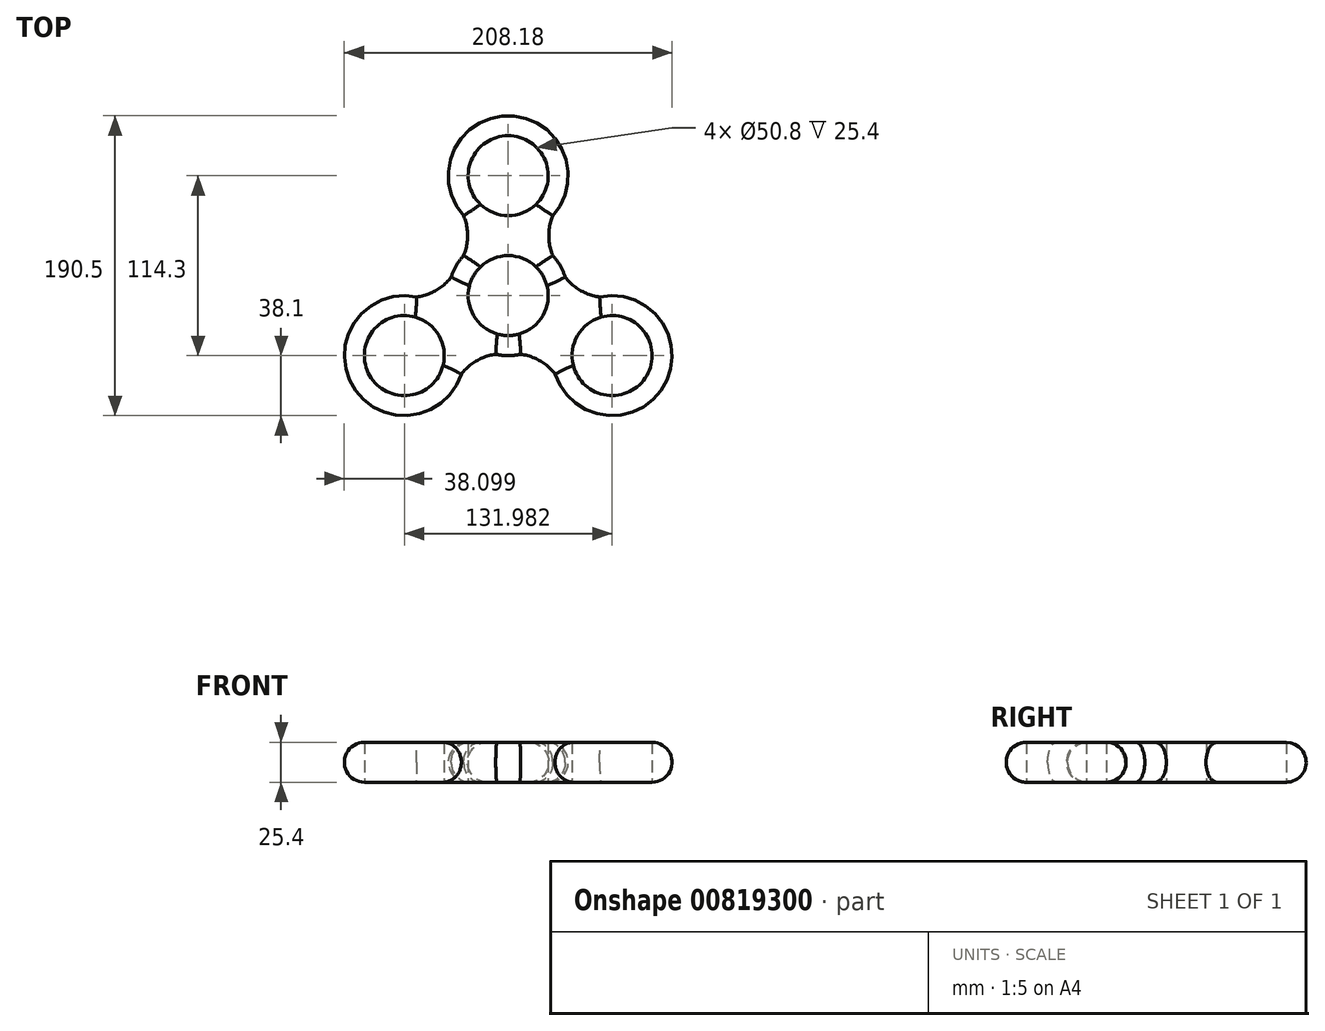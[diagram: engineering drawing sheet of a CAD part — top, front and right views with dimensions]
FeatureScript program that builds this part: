
annotation { "Feature Type Name" : "Feature", "Feature Type Description" : "" }
export const myFeature = defineFeature(function(context is Context, id is Id, definition is map)
    precondition{}
    {
        {
            var Q0;
            Q0=qCreatedBy(makeId("Top.planeOp"),FACE);
            var sketch = newSketch(context, id + "F0", { "sketchPlane" : qUnion([Q0])});
            skCircle(sketch, "E0", {"center": v(0, 0) * mm, "radius": 38.1 * mm});
            skCircle(sketch, "E1", {"center": v(0, 76.2) * mm, "radius": 38.1 * mm});
            skCircle(sketch, "E2.1.0", {"center": v(-66, -38.1) * mm, "radius": 38.1 * mm});
            skCircle(sketch, "E2.2.0", {"center": v(66, -38.1) * mm, "radius": 38.1 * mm});
            skLineSegment(sketch, "E3", {"start": v(0, 38.1) * mm, "end": v(78.67, 38.1) * mm, "construction": true});
            skLineSegment(sketch, "E4", {"start": v(0, 38.1) * mm, "end": v(-78.67, 38.1) * mm, "construction": true});
            skArc(sketch, "E5", {"start": v(28.32, 50.71) * mm, "mid": v(25.78, 38.1) * mm, "end": v(28.32, 25.49) * mm});
            skLineSegment(sketch, "E6", {"start": v(0, 38.1) * mm, "end": v(0, 50.71) * mm, "construction": true});
            skLineSegment(sketch, "E7", {"start": v(0, 50.71) * mm, "end": v(0, 38.1) * mm, "construction": true});
            skLineSegment(sketch, "E8", {"start": v(0, 25.49) * mm, "end": v(0, 38.1) * mm, "construction": true});
            skArc(sketch, "E9", {"start": v(-28.32, 25.49) * mm, "mid": v(-25.78, 38.1) * mm, "end": v(-28.32, 50.71) * mm});
            skArc(sketch, "E10.1.0", {"start": v(-58.08, -0.83) * mm, "mid": v(-45.89, 3.28) * mm, "end": v(-36.23, 11.78) * mm});
            skArc(sketch, "E10.1.1", {"start": v(-7.91, -37.27) * mm, "mid": v(-20.1, -41.38) * mm, "end": v(-29.76, -49.88) * mm});
            skArc(sketch, "E10.2.0", {"start": v(29.76, -49.88) * mm, "mid": v(20.1, -41.38) * mm, "end": v(7.91, -37.27) * mm});
            skArc(sketch, "E10.2.1", {"start": v(36.23, 11.78) * mm, "mid": v(45.89, 3.28) * mm, "end": v(58.08, -0.83) * mm});
            skCircle(sketch, "E11", {"center": v(0, 0) * mm, "radius": 25.4 * mm});
            skCircle(sketch, "E12", {"center": v(0, 76.2) * mm, "radius": 25.4 * mm});
            skCircle(sketch, "E13.1.0", {"center": v(-66, -38.1) * mm, "radius": 25.4 * mm});
            skCircle(sketch, "E13.2.0", {"center": v(66, -38.1) * mm, "radius": 25.4 * mm});
            skSolve(sketch);
        }
        {
            var Q0;
            Q0=makeQuery(id+"F0.imprint","IMPRINT",FACE,{"disambiguationData":[TD([[makeQuery(id+"F0.imprint","IMPRINT",EDGE,{"derivedFrom":sQuery(id+"F0.wireOp",EDGE,"E12")}),-1.0]])]});
            var Q1;
            {var subQ0=sQuery(id+"F0.wireOp",EDGE,"E9");Q1=makeQuery(id+"F0.imprint","IMPRINT",FACE,{"disambiguationData":[TD([[makeQuery(id+"F0.imprint","IMPRINT",EDGE,{"derivedFrom":subQ0}),-1.0]])]});}
            var Q2;
            {var subQ0=sQuery(id+"F0.wireOp",EDGE,"E5");Q2=makeQuery(id+"F0.imprint","IMPRINT",FACE,{"disambiguationData":[TD([[makeQuery(id+"F0.imprint","IMPRINT",EDGE,{"derivedFrom":subQ0}),-1.0]])]});}
            var Q3;
            Q3=makeQuery(id+"F0.imprint","IMPRINT",FACE,{"disambiguationData":[TD([[makeQuery(id+"F0.imprint","IMPRINT",EDGE,{"derivedFrom":sQuery(id+"F0.wireOp",EDGE,"E11")}),-1.0]])]});
            var Q4;
            {var subQ0=sQuery(id+"F0.wireOp",EDGE,"E10.2.1");Q4=makeQuery(id+"F0.imprint","IMPRINT",FACE,{"disambiguationData":[TD([[makeQuery(id+"F0.imprint","IMPRINT",EDGE,{"derivedFrom":subQ0}),-1.0]])]});}
            var Q5;
            {var subQ0=sQuery(id+"F0.wireOp",EDGE,"E10.2.0");Q5=makeQuery(id+"F0.imprint","IMPRINT",FACE,{"disambiguationData":[TD([[makeQuery(id+"F0.imprint","IMPRINT",EDGE,{"derivedFrom":subQ0}),-1.0]])]});}
            var Q6;
            Q6=makeQuery(id+"F0.imprint","IMPRINT",FACE,{"disambiguationData":[TD([[makeQuery(id+"F0.imprint","IMPRINT",EDGE,{"derivedFrom":sQuery(id+"F0.wireOp",EDGE,"E13.2.0")}),-1.0]])]});
            var Q7;
            Q7=makeQuery(id+"F0.imprint","IMPRINT",FACE,{"disambiguationData":[TD([[makeQuery(id+"F0.imprint","IMPRINT",EDGE,{"derivedFrom":sQuery(id+"F0.wireOp",EDGE,"E13.1.0")}),-1.0]])]});
            var Q8;
            {var subQ0=sQuery(id+"F0.wireOp",EDGE,"E10.1.0");Q8=makeQuery(id+"F0.imprint","IMPRINT",FACE,{"disambiguationData":[TD([[makeQuery(id+"F0.imprint","IMPRINT",EDGE,{"derivedFrom":subQ0}),-1.0]])]});}
            var Q9;
            {var subQ0=sQuery(id+"F0.wireOp",EDGE,"E10.1.1");Q9=makeQuery(id+"F0.imprint","IMPRINT",FACE,{"disambiguationData":[TD([[makeQuery(id+"F0.imprint","IMPRINT",EDGE,{"derivedFrom":subQ0}),-1.0]])]});}
            extrude(context, id + "F1", {"entities" : qUnion([Q0, Q1, Q2, Q3, Q4, Q5, Q6, Q7, Q8, Q9]), "depth" : 25.4 * mm, "offsetDistance" : 25.4 * mm});
        }
        {
            var Q0;
            Q0=makeQuery(id+"F1.opExtrude","CAP_EDGE",EDGE,{"disambiguationData":[OSD([sQuery(id+"F0.wireOp",EDGE,"E2.1.0")])],"isStart":false});
            var Q1;
            Q1=makeQuery(id+"F1.opExtrude","CAP_EDGE",EDGE,{"disambiguationData":[OSD([sQuery(id+"F0.wireOp",EDGE,"E10.1.1")])],"isStart":false});
            var Q2;
            {var subQ0=sQuery(id+"F0.wireOp",EDGE,"E0");Q2=makeQuery(id+"F1.opExtrude","CAP_EDGE",EDGE,{"disambiguationData":[OSD([subQ0]),TDD([makeQuery(id+"F0.imprint","IMPRINT",EDGE,{"disambiguationData":[TD([[makeQuery(id+"F0.imprint","INTERSECT",VERTEX,{"derivedFrom":[subQ0,sQuery(id+"F0.wireOp",EDGE,"E10.1.1")]}),-1.0]])],"derivedFrom":subQ0})])],"isStart":false});}
            var Q3;
            Q3=makeQuery(id+"F1.opExtrude","CAP_EDGE",EDGE,{"disambiguationData":[OSD([sQuery(id+"F0.wireOp",EDGE,"E10.2.0")])],"isStart":false});
            var Q4;
            Q4=makeQuery(id+"F1.opExtrude","CAP_EDGE",EDGE,{"disambiguationData":[OSD([sQuery(id+"F0.wireOp",EDGE,"E2.2.0")])],"isStart":false});
            var Q5;
            Q5=makeQuery(id+"F1.opExtrude","CAP_EDGE",EDGE,{"disambiguationData":[OSD([sQuery(id+"F0.wireOp",EDGE,"E10.2.1")])],"isStart":false});
            var Q6;
            {var subQ0=sQuery(id+"F0.wireOp",EDGE,"E0");Q6=makeQuery(id+"F1.opExtrude","CAP_EDGE",EDGE,{"disambiguationData":[OSD([subQ0]),TDD([makeQuery(id+"F0.imprint","IMPRINT",EDGE,{"disambiguationData":[TD([[makeQuery(id+"F0.imprint","INTERSECT",VERTEX,{"derivedFrom":[subQ0,sQuery(id+"F0.wireOp",EDGE,"E5")]}),1.0]])],"derivedFrom":subQ0})])],"isStart":false});}
            var Q7;
            Q7=makeQuery(id+"F1.opExtrude","CAP_EDGE",EDGE,{"disambiguationData":[OSD([sQuery(id+"F0.wireOp",EDGE,"E5")])],"isStart":false});
            var Q8;
            Q8=makeQuery(id+"F1.opExtrude","CAP_EDGE",EDGE,{"disambiguationData":[OSD([sQuery(id+"F0.wireOp",EDGE,"E1")])],"isStart":false});
            var Q9;
            Q9=makeQuery(id+"F1.opExtrude","CAP_EDGE",EDGE,{"disambiguationData":[OSD([sQuery(id+"F0.wireOp",EDGE,"E9")])],"isStart":false});
            var Q10;
            {var subQ0=sQuery(id+"F0.wireOp",EDGE,"E0");Q10=makeQuery(id+"F1.opExtrude","CAP_EDGE",EDGE,{"disambiguationData":[OSD([subQ0]),TDD([makeQuery(id+"F0.imprint","IMPRINT",EDGE,{"disambiguationData":[TD([[makeQuery(id+"F0.imprint","INTERSECT",VERTEX,{"derivedFrom":[subQ0,sQuery(id+"F0.wireOp",EDGE,"E9")]}),-1.0]])],"derivedFrom":subQ0})])],"isStart":false});}
            var Q11;
            Q11=makeQuery(id+"F1.opExtrude","CAP_EDGE",EDGE,{"disambiguationData":[OSD([sQuery(id+"F0.wireOp",EDGE,"E10.1.0")])],"isStart":false});
            var Q12;
            {var subQ0=sQuery(id+"F0.wireOp",EDGE,"E0");Q12=makeQuery(id+"F1.opExtrude","CAP_EDGE",EDGE,{"disambiguationData":[OSD([subQ0]),TDD([makeQuery(id+"F0.imprint","IMPRINT",EDGE,{"disambiguationData":[TD([[makeQuery(id+"F0.imprint","INTERSECT",VERTEX,{"derivedFrom":[subQ0,sQuery(id+"F0.wireOp",EDGE,"E9")]}),-1.0]])],"derivedFrom":subQ0})])],"isStart":true});}
            var Q13;
            Q13=makeQuery(id+"F1.opExtrude","CAP_EDGE",EDGE,{"disambiguationData":[OSD([sQuery(id+"F0.wireOp",EDGE,"E10.1.0")])],"isStart":true});
            var Q14;
            Q14=makeQuery(id+"F1.opExtrude","CAP_EDGE",EDGE,{"disambiguationData":[OSD([sQuery(id+"F0.wireOp",EDGE,"E9")])],"isStart":true});
            var Q15;
            Q15=makeQuery(id+"F1.opExtrude","CAP_EDGE",EDGE,{"disambiguationData":[OSD([sQuery(id+"F0.wireOp",EDGE,"E1")])],"isStart":true});
            var Q16;
            Q16=makeQuery(id+"F1.opExtrude","CAP_EDGE",EDGE,{"disambiguationData":[OSD([sQuery(id+"F0.wireOp",EDGE,"E2.1.0")])],"isStart":true});
            var Q17;
            Q17=makeQuery(id+"F1.opExtrude","CAP_EDGE",EDGE,{"disambiguationData":[OSD([sQuery(id+"F0.wireOp",EDGE,"E10.1.1")])],"isStart":true});
            var Q18;
            {var subQ0=sQuery(id+"F0.wireOp",EDGE,"E0");Q18=makeQuery(id+"F1.opExtrude","CAP_EDGE",EDGE,{"disambiguationData":[OSD([subQ0]),TDD([makeQuery(id+"F0.imprint","IMPRINT",EDGE,{"disambiguationData":[TD([[makeQuery(id+"F0.imprint","INTERSECT",VERTEX,{"derivedFrom":[subQ0,sQuery(id+"F0.wireOp",EDGE,"E10.1.1")]}),-1.0]])],"derivedFrom":subQ0})])],"isStart":true});}
            var Q19;
            Q19=makeQuery(id+"F1.opExtrude","CAP_EDGE",EDGE,{"disambiguationData":[OSD([sQuery(id+"F0.wireOp",EDGE,"E10.2.0")])],"isStart":true});
            var Q20;
            Q20=makeQuery(id+"F1.opExtrude","CAP_EDGE",EDGE,{"disambiguationData":[OSD([sQuery(id+"F0.wireOp",EDGE,"E2.2.0")])],"isStart":true});
            var Q21;
            Q21=makeQuery(id+"F1.opExtrude","CAP_EDGE",EDGE,{"disambiguationData":[OSD([sQuery(id+"F0.wireOp",EDGE,"E10.2.1")])],"isStart":true});
            var Q22;
            {var subQ0=sQuery(id+"F0.wireOp",EDGE,"E0");Q22=makeQuery(id+"F1.opExtrude","CAP_EDGE",EDGE,{"disambiguationData":[OSD([subQ0]),TDD([makeQuery(id+"F0.imprint","IMPRINT",EDGE,{"disambiguationData":[TD([[makeQuery(id+"F0.imprint","INTERSECT",VERTEX,{"derivedFrom":[subQ0,sQuery(id+"F0.wireOp",EDGE,"E5")]}),1.0]])],"derivedFrom":subQ0})])],"isStart":true});}
            var Q23;
            Q23=makeQuery(id+"F1.opExtrude","CAP_EDGE",EDGE,{"disambiguationData":[OSD([sQuery(id+"F0.wireOp",EDGE,"E5")])],"isStart":true});
            fillet(context, id + "F2", {"entities" : qUnion([Q0, Q1, Q2, Q3, Q4, Q5, Q6, Q7, Q8, Q9, Q10, Q11, Q12, Q13, Q14, Q15, Q16, Q17, Q18, Q19, Q20, Q21, Q22, Q23]), "radius" : 12.7 * mm, "tangentPropagation" : true, "allowEdgeOverflow" : false});
        }
    });
